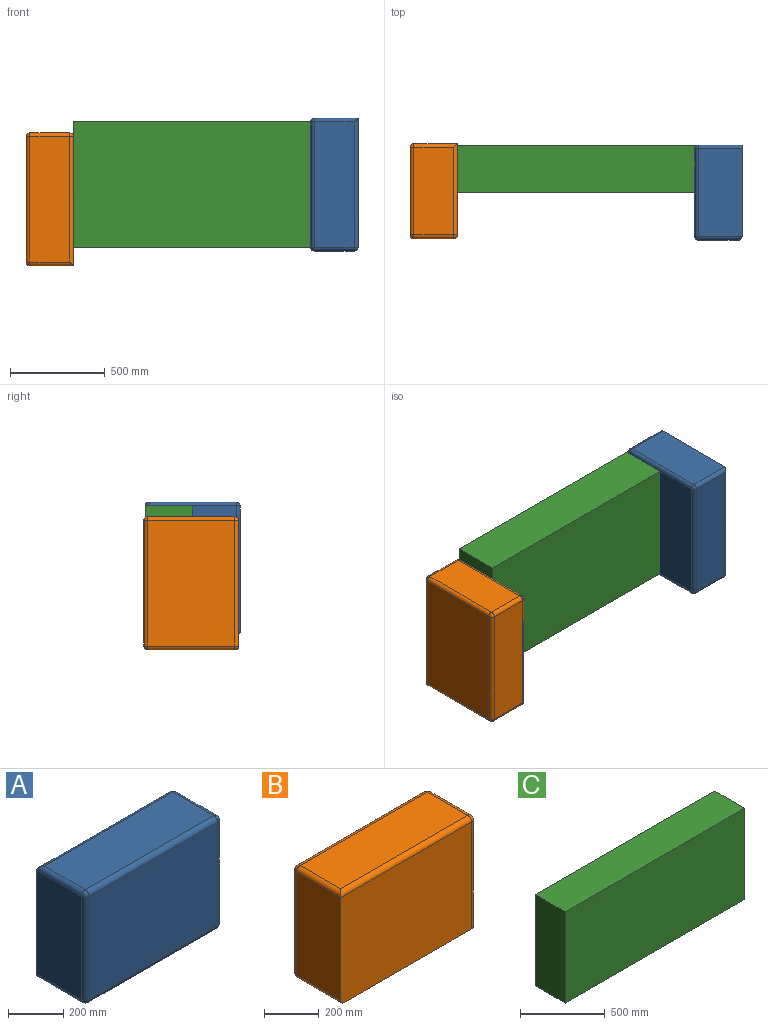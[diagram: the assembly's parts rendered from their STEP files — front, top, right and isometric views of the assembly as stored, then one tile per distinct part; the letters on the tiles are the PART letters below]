
ASSEMBLY  parts=3 mates=2
PART A: 21 faces, bbox 700x250x500 mm
  f0: plane 660x230mm, normal (0,0,-1), area 151800mm2, adj f5,f7,f15,f20
  f1: plane 460x210mm, normal (1,0,0), area 96600mm2, adj f13,f16,f19,f20
  f2: plane 660x210mm, normal (0,0,1), area 138600mm2, adj f9,f10,f13,f14
  f3: plane 460x230mm, normal (-1,0,0), area 105800mm2, adj f5,f7,f8,f10
  f4: plane 660x460mm, normal (0,-1,0), area 303600mm2, adj f8,f9,f15,f16
  f5: plane 680x480mm, normal (0,1,0), area 326314.2mm2, adj f0,f3,f7,f14,f19
  f6: sphere r=20mm, area 628.3mm2, adj f8,f9,f10
  f7: cylinder r=20mm len=230mm, axis (0,1,0), area 7225.7mm2, adj f0,f3,f5,f11
  f8: cylinder r=20mm len=460mm, axis (0,0,1), area 14451.3mm2, adj f3,f4,f6,f11
  f9: cylinder r=20mm len=660mm, axis (1,0,0), area 20734.5mm2, adj f2,f4,f6,f12
  f10: cylinder r=20mm len=230mm, axis (0,-1,0), area 6997.3mm2, adj f2,f3,f6,f14
  f11: sphere r=20mm, area 628.3mm2, adj f7,f8,f15
  f12: sphere r=20mm, area 628.3mm2, adj f9,f13,f16
  f13: cylinder r=20mm len=210mm, axis (0,1,0), area 6597.3mm2, adj f1,f2,f12,f17
  f14: cylinder r=20mm len=680mm, axis (-1,0,0), area 21134.5mm2, adj f2,f5,f10,f17
  f15: cylinder r=20mm len=660mm, axis (-1,0,0), area 20734.5mm2, adj f0,f4,f11,f18
  f16: cylinder r=20mm len=460mm, axis (0,0,-1), area 14451.3mm2, adj f1,f4,f12,f18
  f17: sphere r=20mm, area 628.3mm2, adj f13,f14,f19
  f18: sphere r=20mm, area 628.3mm2, adj f15,f16,f20
  f19: cylinder r=20mm len=480mm, axis (0,0,1), area 14851.3mm2, adj f1,f5,f17,f20
  f20: cylinder r=20mm len=230mm, axis (0,-1,0), area 6997.3mm2, adj f0,f1,f18,f19
PART B: 21 faces, bbox 700x250x500 mm
  f0: plane 660x230mm, normal (0,0,-1), area 151800mm2, adj f4,f10,f17,f20
  f1: plane 460x210mm, normal (1,0,0), area 96600mm2, adj f12,f16,f18,f20
  f2: plane 660x210mm, normal (0,0,1), area 138600mm2, adj f7,f8,f11,f12
  f3: plane 460x230mm, normal (-1,0,0), area 105800mm2, adj f4,f7,f9,f10
  f4: plane 680x480mm, normal (0,-1,0), area 326314.2mm2, adj f0,f3,f10,f11,f18
  f5: plane 660x460mm, normal (0,1,0), area 303600mm2, adj f8,f9,f16,f17
  f6: sphere r=20mm, area 628.3mm2, adj f7,f8,f9
  f7: cylinder r=20mm len=230mm, axis (0,-1,0), area 6997.3mm2, adj f2,f3,f6,f11
  f8: cylinder r=20mm len=660mm, axis (-1,0,0), area 20734.5mm2, adj f2,f5,f6,f13
  f9: cylinder r=20mm len=460mm, axis (0,0,-1), area 14451.3mm2, adj f3,f5,f6,f14
  f10: cylinder r=20mm len=230mm, axis (0,1,0), area 7225.7mm2, adj f0,f3,f4,f14
  f11: cylinder r=20mm len=680mm, axis (1,0,0), area 21134.5mm2, adj f2,f4,f7,f15
  f12: cylinder r=20mm len=210mm, axis (0,1,0), area 6597.3mm2, adj f1,f2,f13,f15
  f13: sphere r=20mm, area 628.3mm2, adj f8,f12,f16
  f14: sphere r=20mm, area 628.3mm2, adj f9,f10,f17
  f15: sphere r=20mm, area 628.3mm2, adj f11,f12,f18
  f16: cylinder r=20mm len=460mm, axis (0,0,1), area 14451.3mm2, adj f1,f5,f13,f19
  f17: cylinder r=20mm len=660mm, axis (1,0,0), area 20734.5mm2, adj f0,f5,f14,f19
  f18: cylinder r=20mm len=480mm, axis (0,0,-1), area 14851.3mm2, adj f1,f4,f15,f20
  f19: sphere r=20mm, area 628.3mm2, adj f16,f17,f20
  f20: cylinder r=20mm len=230mm, axis (0,-1,0), area 6997.3mm2, adj f0,f1,f18,f19
PART C: 6 faces, bbox 1500x250x660 mm
  f0: plane 1500x250mm, normal (0,0,-1), area 375000mm2, adj f1,f3,f4,f5
  f1: plane 660x250mm, normal (1,0,0), area 165000mm2, adj f0,f2,f4,f5
  f2: plane 1500x250mm, normal (0,0,1), area 375000mm2, adj f1,f3,f4,f5
  f3: plane 660x250mm, normal (-1,0,0), area 165000mm2, adj f0,f2,f4,f5
  f4: plane 1500x660mm, normal (0,-1,0), area 990000mm2, adj f0,f1,f2,f3
  f5: plane 1500x660mm, normal (0,1,0), area 990000mm2, adj f0,f1,f2,f3
PLACE A rot(axis=(0.58,0.58,-0.58),120deg) t=(359.73,-29.99,-55.07)mm
PLACE B rot(axis=(0.58,-0.58,0.58),120deg) t=(-1390.27,-22.5,-135.92)mm
PLACE C t=(-390.27,220.01,-56.49)mm
MATE planar A.f5 <-> C.f1  axis (1,0,0) through (359.73,220.01,-56.49)mm
MATE planar B.f4 <-> C.f3  axis (1,0,0) through (-1140.27,227.5,-134.49)mm
